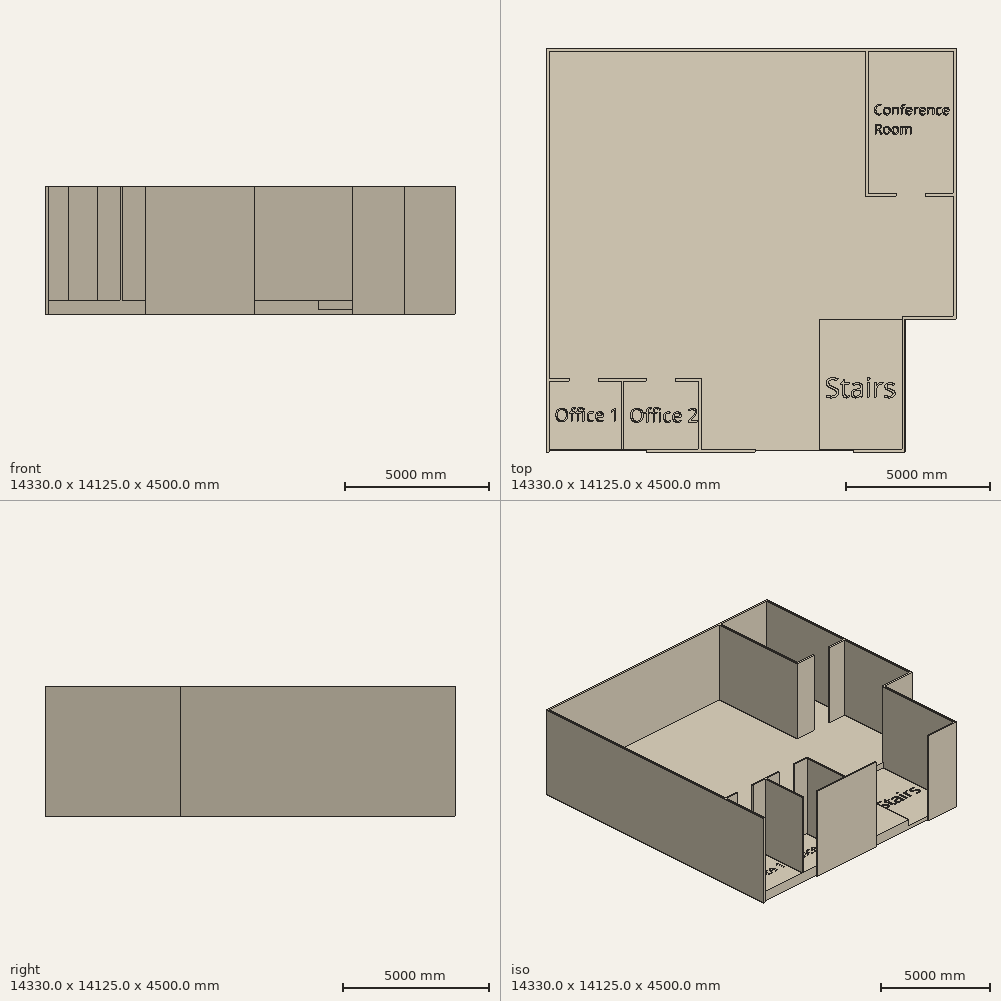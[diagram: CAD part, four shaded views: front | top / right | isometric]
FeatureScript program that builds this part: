
annotation { "Feature Type Name" : "Feature", "Feature Type Description" : "" }
export const myFeature = defineFeature(function(context is Context, id is Id, definition is map)
    precondition{}
    {
        {
            var Q0;
            Q0=qCreatedBy(makeId("Top.planeOp"),FACE);
            var sketch = newSketch(context, id + "F0", { "sketchPlane" : qUnion([Q0])});
            skLineSegment(sketch, "E0.bottom", {"start": v(7165, -7062.5) * mm, "end": v(-7165, -7062.5) * mm});
            skLineSegment(sketch, "E0.top", {"start": v(7165, 7062.5) * mm, "end": v(-7165, 7062.5) * mm});
            skLineSegment(sketch, "E0.left", {"start": v(7165, -7062.5) * mm, "end": v(7165, 7062.5) * mm});
            skLineSegment(sketch, "E0.right", {"start": v(-7165, -7062.5) * mm, "end": v(-7165, 7062.5) * mm});
            skPoint(sketch, "E0.middle", {"position": v(0, 0) * mm});
            skSolve(sketch);
        }
        {
            var Q0;
            Q0 = qSketchRegion(id + "F0", true);
            extrude(context, id + "F1", {"entities" : qUnion([Q0]), "depth" : 500 * mm, "offsetDistance" : 25 * mm});
        }
        {
            var Q0;
            Q0=makeQuery(id+"F1.opExtrude","CAP_FACE",FACE,{"disambiguationData":[OSD([sQuery(id+"F0.wireOp",EDGE,"E0.bottom"),sQuery(id+"F0.wireOp",EDGE,"E0.top"),sQuery(id+"F0.wireOp",EDGE,"E0.left"),sQuery(id+"F0.wireOp",EDGE,"E0.right")])],"isStart":false});
            var sketch = newSketch(context, id + "F2", { "sketchPlane" : qUnion([Q0])});
            skLineSegment(sketch, "E1.bottom", {"start": v(-7165, 7062.5) * mm, "end": v(7165, 7062.5) * mm});
            skLineSegment(sketch, "E1.top", {"start": v(-7075, 6972.5) * mm, "end": v(7075, 6972.5) * mm});
            skLineSegment(sketch, "E1.left", {"start": v(-7165, 7062.5) * mm, "end": v(-7165, 6972.5) * mm});
            skLineSegment(sketch, "E1.right", {"start": v(7165, 7062.5) * mm, "end": v(7165, 6972.5) * mm});
            skLineSegment(sketch, "E2.top", {"start": v(7165, -7062.5) * mm, "end": v(7075, -7062.5) * mm});
            skLineSegment(sketch, "E2.left", {"start": v(7165, 6972.5) * mm, "end": v(7165, -7062.5) * mm});
            skLineSegment(sketch, "E2.right", {"start": v(7075, 6972.5) * mm, "end": v(7075, -6972.5) * mm});
            skLineSegment(sketch, "E3.bottom", {"start": v(7075, -7062.5) * mm, "end": v(-7165, -7062.5) * mm});
            skLineSegment(sketch, "E3.top", {"start": v(7075, -6972.5) * mm, "end": v(-7075, -6972.5) * mm});
            skLineSegment(sketch, "E3.right", {"start": v(-7165, -7062.5) * mm, "end": v(-7165, -6972.5) * mm});
            skLineSegment(sketch, "E4.left", {"start": v(-7165, -6972.5) * mm, "end": v(-7165, 6847.5) * mm});
            skLineSegment(sketch, "E4.right", {"start": v(-7075, -6972.5) * mm, "end": v(-7075, 6972.5) * mm});
            skLineSegment(sketch, "E5", {"start": v(-7165, 6847.5) * mm, "end": v(-7165, 6972.5) * mm});
            skSolve(sketch);
        }
        {
            var Q0;
            Q0 = qSketchRegion(id + "F2", true);
            extrude(context, id + "F3", {"entities" : qUnion([Q0]), "operationType" : NewBodyOperationType.ADD, "depth" : 4000 * mm, "offsetDistance" : 25 * mm});
        }
        {
            var Q0;
            Q0=makeQuery(id+"F3.opExtrude","CAP_FACE",FACE,{"disambiguationData":[OSD([sQuery(id+"F2.wireOp",EDGE,"E1.bottom"),sQuery(id+"F2.wireOp",EDGE,"E1.top"),sQuery(id+"F2.wireOp",EDGE,"E1.left"),sQuery(id+"F2.wireOp",EDGE,"E1.right"),sQuery(id+"F2.wireOp",EDGE,"E2.top"),sQuery(id+"F2.wireOp",EDGE,"E2.left"),sQuery(id+"F2.wireOp",EDGE,"E2.right"),sQuery(id+"F2.wireOp",EDGE,"E3.bottom"),sQuery(id+"F2.wireOp",EDGE,"E3.top"),sQuery(id+"F2.wireOp",EDGE,"E3.right"),sQuery(id+"F2.wireOp",EDGE,"E4.left"),sQuery(id+"F2.wireOp",EDGE,"E4.right"),sQuery(id+"F2.wireOp",EDGE,"E5")])],"isStart":false});
            var sketch = newSketch(context, id + "F4", { "sketchPlane" : qUnion([Q0])});
            skLineSegment(sketch, "E6.bottom", {"start": v(-7075, -6972.5) * mm, "end": v(-3675, -6972.5) * mm});
            skLineSegment(sketch, "E6.top", {"start": v(-7075, -7062.5) * mm, "end": v(-3675, -7062.5) * mm});
            skLineSegment(sketch, "E6.left", {"start": v(-7075, -6972.5) * mm, "end": v(-7075, -7062.5) * mm});
            skLineSegment(sketch, "E6.right", {"start": v(-3675, -6972.5) * mm, "end": v(-3675, -7062.5) * mm});
            skLineSegment(sketch, "E7.bottom", {"start": v(150, -6972.5) * mm, "end": v(3550, -6972.5) * mm});
            skLineSegment(sketch, "E7.top", {"start": v(150, -7062.5) * mm, "end": v(3550, -7062.5) * mm});
            skLineSegment(sketch, "E7.left", {"start": v(150, -6972.5) * mm, "end": v(150, -7062.5) * mm});
            skLineSegment(sketch, "E7.right", {"start": v(3550, -6972.5) * mm, "end": v(3550, -7062.5) * mm});
            skSolve(sketch);
        }
        {
            var Q0;
            Q0 = qSketchRegion(id + "F4", true);
            extrude(context, id + "F5", {"entities" : qUnion([Q0]), "operationType" : NewBodyOperationType.REMOVE, "oppositeDirection" : true, "depth" : 4820 * mm, "offsetDistance" : 25 * mm});
        }
        {
            var Q0;
            Q0=makeQuery(id+"F1.opExtrude","CAP_FACE",FACE,{"disambiguationData":[OSD([sQuery(id+"F0.wireOp",EDGE,"E0.bottom"),sQuery(id+"F0.wireOp",EDGE,"E0.top"),sQuery(id+"F0.wireOp",EDGE,"E0.left"),sQuery(id+"F0.wireOp",EDGE,"E0.right")])],"isStart":false});
            var sketch = newSketch(context, id + "F6", { "sketchPlane" : qUnion([Q0])});
            skLineSegment(sketch, "E8.bottom", {"start": v(5365, -6972.5) * mm, "end": v(2365, -6972.5) * mm});
            skLineSegment(sketch, "E8.top", {"start": v(5365, -2402.5) * mm, "end": v(2365, -2402.5) * mm});
            skLineSegment(sketch, "E8.left", {"start": v(5365, -6972.5) * mm, "end": v(5365, -2402.5) * mm});
            skLineSegment(sketch, "E8.right", {"start": v(2365, -6972.5) * mm, "end": v(2365, -2402.5) * mm});
            skSolve(sketch);
        }
        {
            var Q0;
            Q0 = qSketchRegion(id + "F6", true);
            extrude(context, id + "F7", {"entities" : qUnion([Q0]), "operationType" : NewBodyOperationType.REMOVE, "oppositeDirection" : true, "depth" : 310 * mm, "offsetDistance" : 25 * mm});
        }
        {
            var Q0;
            Q0=makeQuery(id+"F1.opExtrude","CAP_FACE",FACE,{"disambiguationData":[OSD([sQuery(id+"F0.wireOp",EDGE,"E0.bottom"),sQuery(id+"F0.wireOp",EDGE,"E0.top"),sQuery(id+"F0.wireOp",EDGE,"E0.left"),sQuery(id+"F0.wireOp",EDGE,"E0.right")])],"isStart":false});
            var sketch = newSketch(context, id + "F8", { "sketchPlane" : qUnion([Q0])});
            skLineSegment(sketch, "E9.bottom", {"start": v(5365, -2402.5) * mm, "end": v(7261.47, -2402.5) * mm});
            skLineSegment(sketch, "E9.top", {"start": v(5365, -7185.88) * mm, "end": v(7261.47, -7185.88) * mm});
            skLineSegment(sketch, "E9.left", {"start": v(5365, -2402.5) * mm, "end": v(5365, -7185.88) * mm});
            skLineSegment(sketch, "E9.right", {"start": v(7261.47, -2402.5) * mm, "end": v(7261.47, -7185.88) * mm});
            skSolve(sketch);
        }
        {
            var Q0;
            Q0 = qSketchRegion(id + "F8", true);
            extrude(context, id + "F9", {"entities" : qUnion([Q0]), "operationType" : NewBodyOperationType.REMOVE, "oppositeDirection" : true, "depth" : 1900 * mm, "offsetDistance" : 25 * mm, "hasSecondDirection" : true, "secondDirectionOppositeDirection" : false, "secondDirectionDepth" : 5000 * mm});
        }
        {
            var Q0;
            Q0=makeQuery(id+"F1.opExtrude","CAP_FACE",FACE,{"disambiguationData":[OSD([sQuery(id+"F0.wireOp",EDGE,"E0.bottom"),sQuery(id+"F0.wireOp",EDGE,"E0.top"),sQuery(id+"F0.wireOp",EDGE,"E0.left"),sQuery(id+"F0.wireOp",EDGE,"E0.right")])],"isStart":false});
            var sketch = newSketch(context, id + "F10", { "sketchPlane" : qUnion([Q0])});
            skLineSegment(sketch, "E10.bottom", {"start": v(7075, -2402.5) * mm, "end": v(5365, -2402.5) * mm});
            skLineSegment(sketch, "E10.top", {"start": v(7075, -2312.5) * mm, "end": v(5365, -2312.5) * mm});
            skLineSegment(sketch, "E10.left", {"start": v(7075, -2402.5) * mm, "end": v(7075, -2312.5) * mm});
            skLineSegment(sketch, "E11.bottom", {"start": v(5365, -2312.5) * mm, "end": v(5275, -2312.5) * mm});
            skLineSegment(sketch, "E11.top", {"start": v(5365, -7036.17) * mm, "end": v(5275, -7036.17) * mm});
            skLineSegment(sketch, "E11.left", {"start": v(5365, -2402.5) * mm, "end": v(5365, -7036.17) * mm});
            skLineSegment(sketch, "E11.right", {"start": v(5275, -2312.5) * mm, "end": v(5275, -7036.17) * mm});
            skSolve(sketch);
        }
        {
            var Q0;
            Q0 = qSketchRegion(id + "F10", true);
            extrude(context, id + "F11", {"entities" : qUnion([Q0]), "operationType" : NewBodyOperationType.ADD, "depth" : 4000 * mm, "offsetDistance" : 25 * mm, "hasSecondDirection" : true, "secondDirectionOppositeDirection" : true, "secondDirectionDepth" : 440 * mm});
        }
        {
            var Q0;
            Q0=makeQuery(id+"F1.opExtrude","CAP_FACE",FACE,{"disambiguationData":[OSD([sQuery(id+"F0.wireOp",EDGE,"E0.bottom"),sQuery(id+"F0.wireOp",EDGE,"E0.top"),sQuery(id+"F0.wireOp",EDGE,"E0.left"),sQuery(id+"F0.wireOp",EDGE,"E0.right")])],"isStart":false});
            var sketch = newSketch(context, id + "F12", { "sketchPlane" : qUnion([Q0])});
            skLineSegment(sketch, "E12.top", {"start": v(7075, 1992.75) * mm, "end": v(4075, 1992.75) * mm});
            skLineSegment(sketch, "E12.right", {"start": v(4075, 6992.75) * mm, "end": v(4075, 1992.75) * mm});
            skLineSegment(sketch, "E13", {"start": v(4075, 6992.75) * mm, "end": v(3985, 6972.5) * mm});
            skLineSegment(sketch, "E14", {"start": v(3985, 6972.5) * mm, "end": v(3985, 1902.75) * mm});
            skLineSegment(sketch, "E15", {"start": v(3985, 1902.75) * mm, "end": v(7075, 1902.75) * mm});
            skLineSegment(sketch, "E16", {"start": v(7075, 1902.75) * mm, "end": v(7075, 1992.75) * mm});
            skSolve(sketch);
        }
        {
            var Q0;
            Q0 = qSketchRegion(id + "F12", true);
            extrude(context, id + "F13", {"entities" : qUnion([Q0]), "operationType" : NewBodyOperationType.ADD, "depth" : 4000 * mm, "offsetDistance" : 25 * mm});
        }
        {
            var Q0;
            Q0=makeQuery(id+"F13.boolean.opBoolean","SPLIT",FACE,{"disambiguationData":[TD([makeQuery(id+"F3.opExtrude","SWEPT_FACE",FACE,{"disambiguationData":[OSD([sQuery(id+"F2.wireOp",EDGE,"E3.top")])]})])],"derivedFrom":makeQuery(id+"F1.opExtrude","CAP_FACE",FACE,{"disambiguationData":[OSD([sQuery(id+"F0.wireOp",EDGE,"E0.bottom"),sQuery(id+"F0.wireOp",EDGE,"E0.top"),sQuery(id+"F0.wireOp",EDGE,"E0.left"),sQuery(id+"F0.wireOp",EDGE,"E0.right")])],"isStart":false})});
            var sketch = newSketch(context, id + "F14", { "sketchPlane" : qUnion([Q0])});
            skLineSegment(sketch, "E17", {"start": v(-7075, -4562.5) * mm, "end": v(-4553.75, -4562.5) * mm});
            skLineSegment(sketch, "E18", {"start": v(-1852.5, -4562.5) * mm, "end": v(-1852.5, -6972.5) * mm});
            skLineSegment(sketch, "E19", {"start": v(-1852.5, -6972.5) * mm, "end": v(-1762.5, -6972.5) * mm});
            skLineSegment(sketch, "E20", {"start": v(-1762.5, -6972.5) * mm, "end": v(-1762.5, -4472.5) * mm});
            skLineSegment(sketch, "E21", {"start": v(-1762.5, -4472.5) * mm, "end": v(-7075, -4472.5) * mm});
            skLineSegment(sketch, "E22", {"start": v(-7075, -4472.5) * mm, "end": v(-7075, -4562.5) * mm});
            skLineSegment(sketch, "E23", {"start": v(-4463.75, -4562.5) * mm, "end": v(-4463.75, -6972.5) * mm});
            skLineSegment(sketch, "E24", {"start": v(-4463.75, -6972.5) * mm, "end": v(-4553.75, -6972.5) * mm});
            skLineSegment(sketch, "E25", {"start": v(-4553.75, -6972.5) * mm, "end": v(-4553.75, -4562.5) * mm});
            skLineSegment(sketch, "E26.trimOffspring", {"start": v(-4463.75, -4562.5) * mm, "end": v(-1852.5, -4562.5) * mm});
            skSolve(sketch);
        }
        {
            var Q0;
            Q0 = qSketchRegion(id + "F14", true);
            extrude(context, id + "F15", {"entities" : qUnion([Q0]), "operationType" : NewBodyOperationType.ADD, "depth" : 4000 * mm, "offsetDistance" : 25 * mm});
        }
        {
            var Q0;
            {var subQ1=sQuery(id+"F2.wireOp",EDGE,"E3.top");var subQ2=makeQuery(id+"F3.opExtrude","SWEPT_FACE",FACE,{"disambiguationData":[OSD([subQ1])]});var subQ3=sQuery(id+"F2.wireOp",EDGE,"E3.bottom");var subQ4=sQuery(id+"F2.wireOp",EDGE,"E2.top");var subQ7=sQuery(id+"F2.wireOp",EDGE,"E2.right");var subQ9=sQuery(id+"F2.wireOp",EDGE,"E2.left");var subQ10=sQuery(id+"F2.wireOp",EDGE,"E1.right");var subQ12=sQuery(id+"F2.wireOp",EDGE,"E1.bottom");var subQ15=sQuery(id+"F2.wireOp",EDGE,"E5");var subQ16=sQuery(id+"F2.wireOp",EDGE,"E4.left");var subQ17=sQuery(id+"F2.wireOp",EDGE,"E3.right");var subQ18=sQuery(id+"F2.wireOp",EDGE,"E1.left");var subQ21=makeQuery(id+"F1.opExtrude","SWEPT_FACE",FACE,{"disambiguationData":[OSD([sQuery(id+"F0.wireOp",EDGE,"E0.top")])]});var subQ22=sQuery(id+"F2.wireOp",EDGE,"E1.top");var subQ24=sQuery(id+"F2.wireOp",EDGE,"E4.right");var subQ27=makeQuery(id+"F3.opExtrude","CAP_FACE",FACE,{"disambiguationData":[OSD([subQ12,subQ22,subQ18,subQ10,subQ4,subQ9,subQ7,subQ3,subQ1,subQ17,subQ16,subQ24,subQ15])],"isStart":false});var subQ28=makeQuery(id+"F5.boolean.opBoolean","SPLIT",FACE,{"disambiguationData":[TD([subQ21])],"derivedFrom":subQ27});Q0=makeQuery(id+"F15.boolean.opBoolean","MERGE",FACE,{"derivedFrom":[makeQuery(id+"F5.boolean.opBoolean","SPLIT",FACE,{"disambiguationData":[TD([makeQuery(id+"F5.opExtrude","SWEPT_FACE",FACE,{"disambiguationData":[OSD([sQuery(id+"F4.wireOp",EDGE,"E6.right")])]})])],"derivedFrom":subQ27}),makeQuery(id+"F13.boolean.opBoolean","MERGE",FACE,{"derivedFrom":[makeQuery(id+"F11.boolean.opBoolean","MERGE",FACE,{"derivedFrom":[makeQuery(id+"F9.boolean.opBoolean","SPLIT",FACE,{"disambiguationData":[TD([subQ21])],"derivedFrom":subQ28}),makeQuery(id+"F9.boolean.opBoolean","SPLIT",FACE,{"disambiguationData":[TD([subQ2])],"derivedFrom":subQ28}),makeQuery(id+"F11.opExtrude","CAP_FACE",FACE,{"disambiguationData":[OSD([sQuery(id+"F10.wireOp",EDGE,"E10.bottom"),sQuery(id+"F10.wireOp",EDGE,"E10.top"),sQuery(id+"F10.wireOp",EDGE,"E10.left"),sQuery(id+"F10.wireOp",EDGE,"E11.bottom"),sQuery(id+"F10.wireOp",EDGE,"E11.top"),sQuery(id+"F10.wireOp",EDGE,"E11.left"),sQuery(id+"F10.wireOp",EDGE,"E11.right")])],"isStart":false})]}),makeQuery(id+"F13.opExtrude","CAP_FACE",FACE,{"disambiguationData":[OSD([sQuery(id+"F12.wireOp",EDGE,"E12.top"),sQuery(id+"F12.wireOp",EDGE,"E12.right"),sQuery(id+"F12.wireOp",EDGE,"E13"),sQuery(id+"F12.wireOp",EDGE,"E14"),sQuery(id+"F12.wireOp",EDGE,"E15"),sQuery(id+"F12.wireOp",EDGE,"E16")])],"isStart":false})]}),makeQuery(id+"F15.opExtrude","CAP_FACE",FACE,{"disambiguationData":[OSD([sQuery(id+"F14.wireOp",EDGE,"E17"),sQuery(id+"F14.wireOp",EDGE,"E18"),sQuery(id+"F14.wireOp",EDGE,"E19"),sQuery(id+"F14.wireOp",EDGE,"E20"),sQuery(id+"F14.wireOp",EDGE,"E21"),sQuery(id+"F14.wireOp",EDGE,"E22"),sQuery(id+"F14.wireOp",EDGE,"E23"),sQuery(id+"F14.wireOp",EDGE,"E24"),sQuery(id+"F14.wireOp",EDGE,"E25"),sQuery(id+"F14.wireOp",EDGE,"E26.trimOffspring")])],"isStart":false})]});}
            var sketch = newSketch(context, id + "F16", { "sketchPlane" : qUnion([Q0])});
            skLineSegment(sketch, "E27.bottom", {"start": v(-6353.75, -4472.5) * mm, "end": v(-5353.75, -4472.5) * mm});
            skLineSegment(sketch, "E27.top", {"start": v(-6353.75, -4562.5) * mm, "end": v(-5353.75, -4562.5) * mm});
            skLineSegment(sketch, "E27.left", {"start": v(-6353.75, -4472.5) * mm, "end": v(-6353.75, -4562.5) * mm});
            skLineSegment(sketch, "E27.right", {"start": v(-5353.75, -4472.5) * mm, "end": v(-5353.75, -4562.5) * mm});
            skLineSegment(sketch, "E28.bottom", {"start": v(-3652.5, -4562.5) * mm, "end": v(-2652.5, -4562.5) * mm});
            skLineSegment(sketch, "E28.top", {"start": v(-3652.5, -4472.5) * mm, "end": v(-2652.5, -4472.5) * mm});
            skLineSegment(sketch, "E28.left", {"start": v(-3652.5, -4562.5) * mm, "end": v(-3652.5, -4472.5) * mm});
            skLineSegment(sketch, "E28.right", {"start": v(-2652.5, -4562.5) * mm, "end": v(-2652.5, -4472.5) * mm});
            skLineSegment(sketch, "E29.bottom", {"start": v(5075, 1992.75) * mm, "end": v(6075, 1992.75) * mm});
            skLineSegment(sketch, "E29.top", {"start": v(5075, 1902.75) * mm, "end": v(6075, 1902.75) * mm});
            skLineSegment(sketch, "E29.left", {"start": v(5075, 1992.75) * mm, "end": v(5075, 1902.75) * mm});
            skLineSegment(sketch, "E29.right", {"start": v(6075, 1992.75) * mm, "end": v(6075, 1902.75) * mm});
            skSolve(sketch);
        }
        {
            var Q0;
            Q0 = qSketchRegion(id + "F16", true);
            extrude(context, id + "F17", {"entities" : qUnion([Q0]), "operationType" : NewBodyOperationType.REMOVE, "oppositeDirection" : true, "depth" : 4000 * mm, "offsetDistance" : 25 * mm});
        }
        {
            var Q0;
            {var subQ4=makeQuery(id+"F3.opExtrude","SWEPT_FACE",FACE,{"disambiguationData":[OSD([sQuery(id+"F2.wireOp",EDGE,"E1.top")])]});var subQ7=makeQuery(id+"F3.opExtrude","SWEPT_FACE",FACE,{"disambiguationData":[OSD([sQuery(id+"F2.wireOp",EDGE,"E3.top")])]});var subQ14=makeQuery(id+"F5.boolean.opBoolean","COPY",FACE,{"derivedFrom":makeQuery(id+"F5.opExtrude","SWEPT_FACE",FACE,{"disambiguationData":[OSD([sQuery(id+"F4.wireOp",EDGE,"E6.right")])]})});var subQ16=makeQuery(id+"F1.opExtrude","CAP_FACE",FACE,{"disambiguationData":[OSD([sQuery(id+"F0.wireOp",EDGE,"E0.bottom"),sQuery(id+"F0.wireOp",EDGE,"E0.top"),sQuery(id+"F0.wireOp",EDGE,"E0.left"),sQuery(id+"F0.wireOp",EDGE,"E0.right")])],"isStart":false});var subQ17=makeQuery(id+"F13.boolean.opBoolean","SPLIT",FACE,{"disambiguationData":[TD([subQ7])],"derivedFrom":subQ16});Q0=makeQuery(id+"F17.boolean.opBoolean","MERGE",FACE,{"derivedFrom":[makeQuery(id+"F13.boolean.opBoolean","SPLIT",FACE,{"disambiguationData":[TD([makeQuery(id+"F13.opExtrude","SWEPT_FACE",FACE,{"disambiguationData":[OSD([sQuery(id+"F12.wireOp",EDGE,"E12.top")])]})])],"derivedFrom":subQ16}),makeQuery(id+"F15.boolean.opBoolean","SPLIT",FACE,{"disambiguationData":[TD([makeQuery(id+"F15.opExtrude","SWEPT_FACE",FACE,{"disambiguationData":[OSD([sQuery(id+"F14.wireOp",EDGE,"E17")])]})])],"derivedFrom":subQ17}),makeQuery(id+"F15.boolean.opBoolean","SPLIT",FACE,{"disambiguationData":[TD([subQ14])],"derivedFrom":subQ17}),makeQuery(id+"F15.boolean.opBoolean","SPLIT",FACE,{"disambiguationData":[TD([subQ4])],"derivedFrom":subQ17}),makeQuery(id+"F17.opExtrude","CAP_FACE",FACE,{"disambiguationData":[OSD([sQuery(id+"F16.wireOp",EDGE,"E27.bottom"),sQuery(id+"F16.wireOp",EDGE,"E27.top"),sQuery(id+"F16.wireOp",EDGE,"E27.left"),sQuery(id+"F16.wireOp",EDGE,"E27.right")])],"isStart":false}),makeQuery(id+"F17.opExtrude","CAP_FACE",FACE,{"disambiguationData":[OSD([sQuery(id+"F16.wireOp",EDGE,"E28.bottom"),sQuery(id+"F16.wireOp",EDGE,"E28.top"),sQuery(id+"F16.wireOp",EDGE,"E28.left"),sQuery(id+"F16.wireOp",EDGE,"E28.right")])],"isStart":false}),makeQuery(id+"F17.opExtrude","CAP_FACE",FACE,{"disambiguationData":[OSD([sQuery(id+"F16.wireOp",EDGE,"E29.bottom"),sQuery(id+"F16.wireOp",EDGE,"E29.top"),sQuery(id+"F16.wireOp",EDGE,"E29.left"),sQuery(id+"F16.wireOp",EDGE,"E29.right")])],"isStart":false})]});}
            var sketch = newSketch(context, id + "F18", { "sketchPlane" : qUnion([Q0])});
            skText(sketch, "E30", { "text": "Conference \nRoom", "fontName": "OpenSans-Regular.ttf"});
            skText(sketch, "E31", { "text": "Office 1", "fontName": "OpenSans-Regular.ttf"});
            skText(sketch, "E32", { "text": "Office 2\n", "fontName": "OpenSans-Regular.ttf"});
            const initialGuessF18  = {"E30": [4.275, 4.73664, 1, 0, 0.35699], "E31": [-6.875, -5.9822, 1, 0, 0.45894], "E32": [-4.26375, -6.00842, 1, 0, 0.48517]};
            skSetInitialGuess(sketch, initialGuessF18);
            skSolve(sketch);
        }
        {
            var Q0;
            Q0 = qSketchRegion(id + "F18", true);
            extrude(context, id + "F19", {"entities" : qUnion([Q0]), "operationType" : NewBodyOperationType.REMOVE, "oppositeDirection" : true, "depth" : 120 * mm, "offsetDistance" : 25 * mm});
        }
        {
            var Q0;
            Q0=makeQuery(id+"F7.boolean.opBoolean","COPY",FACE,{"derivedFrom":makeQuery(id+"F7.opExtrude","CAP_FACE",FACE,{"disambiguationData":[OSD([sQuery(id+"F6.wireOp",EDGE,"E8.bottom"),sQuery(id+"F6.wireOp",EDGE,"E8.top"),sQuery(id+"F6.wireOp",EDGE,"E8.left"),sQuery(id+"F6.wireOp",EDGE,"E8.right")])],"isStart":false})});
            var sketch = newSketch(context, id + "F20", { "sketchPlane" : qUnion([Q0])});
            skText(sketch, "E33", { "text": "Stairs", "fontName": "OpenSans-Regular.ttf"});
            const initialGuessF20  = {"E33": [2.565, -5.14726, 1, 0, 0.69572]};
            skSetInitialGuess(sketch, initialGuessF20);
            skSolve(sketch);
        }
        {
            var Q0;
            Q0 = qSketchRegion(id + "F20", true);
            extrude(context, id + "F21", {"entities" : qUnion([Q0]), "operationType" : NewBodyOperationType.REMOVE, "oppositeDirection" : true, "depth" : 25 * mm, "offsetDistance" : 25 * mm});
        }
    });
